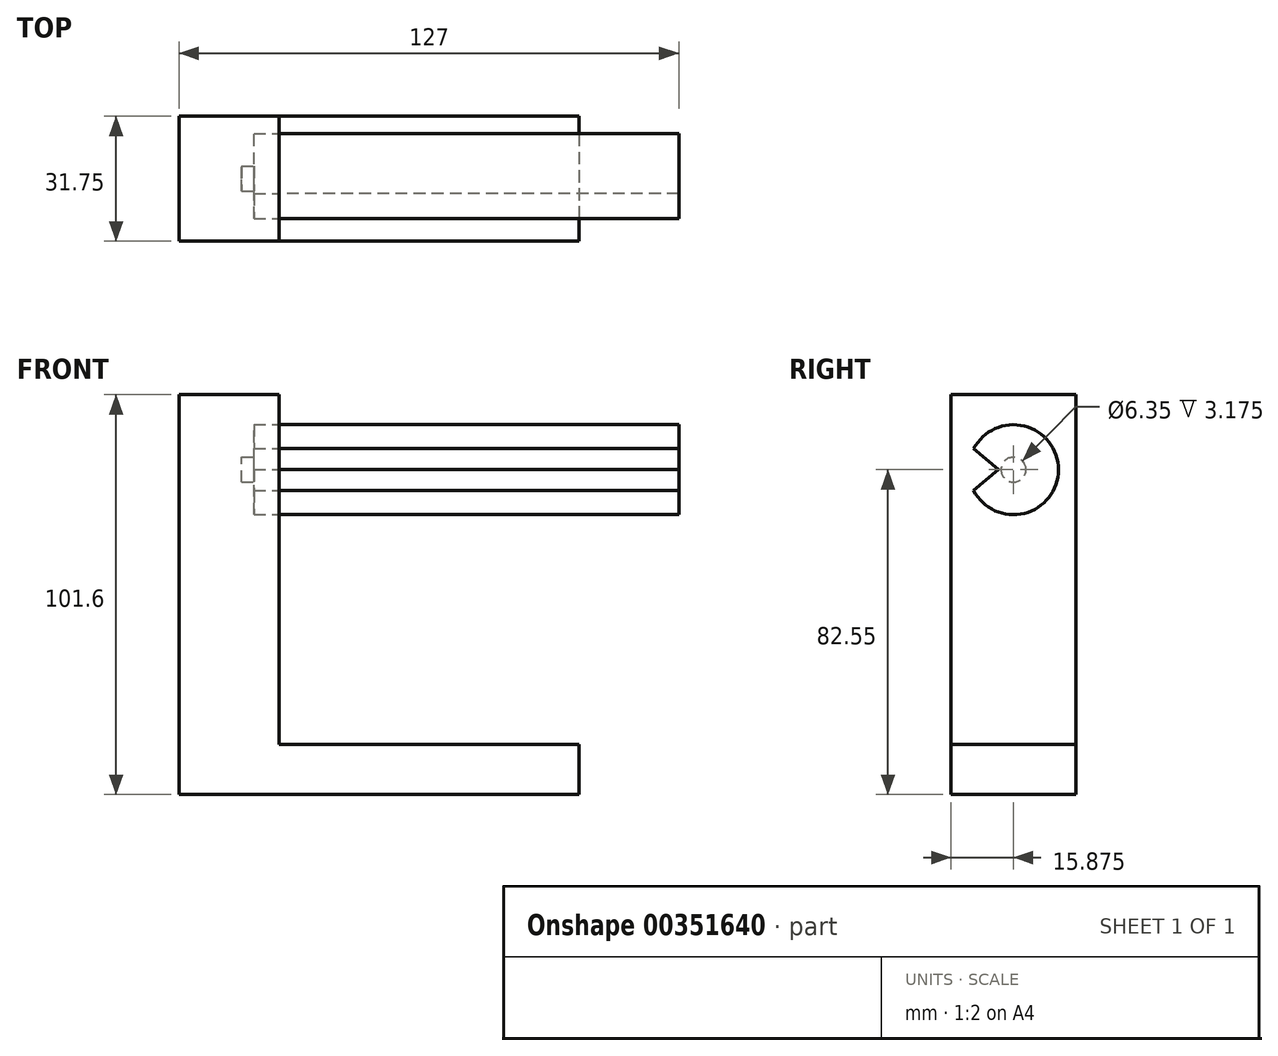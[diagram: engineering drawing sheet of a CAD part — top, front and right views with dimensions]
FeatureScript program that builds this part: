
annotation { "Feature Type Name" : "Feature", "Feature Type Description" : "" }
export const myFeature = defineFeature(function(context is Context, id is Id, definition is map)
    precondition{}
    {
        {
            var Q0;
            Q0=qCreatedBy(makeId("Right.planeOp"),FACE);
            var sketch = newSketch(context, id + "F0", { "sketchPlane" : qUnion([Q0])});
            skLineSegment(sketch, "E0.bottom", {"start": v(0, 0) * mm, "end": v(31.75, 0) * mm});
            skLineSegment(sketch, "E0.top", {"start": v(0, 101.6) * mm, "end": v(31.75, 101.6) * mm});
            skLineSegment(sketch, "E0.left", {"start": v(0, 0) * mm, "end": v(0, 101.6) * mm});
            skLineSegment(sketch, "E0.right", {"start": v(31.75, 0) * mm, "end": v(31.75, 101.6) * mm});
            skSolve(sketch);
        }
        {
            var Q0;
            Q0=qSketchRegion(id+"F0",true);
            extrude(context, id + "F1", {"entities" : qUnion([Q0]), "oppositeDirection" : true, "depth" : 25.4 * mm});
        }
        {
            var Q0;
            Q0=makeQuery(id+"F1.opExtrude","CAP_FACE",FACE,{"disambiguationData":[OSD([sQuery(id+"F0.wireOp",EDGE,"E0.bottom"),sQuery(id+"F0.wireOp",EDGE,"E0.top"),sQuery(id+"F0.wireOp",EDGE,"E0.left"),sQuery(id+"F0.wireOp",EDGE,"E0.right")])],"isStart":true});
            var sketch = newSketch(context, id + "F2", { "sketchPlane" : qUnion([Q0])});
            skArc(sketch, "E1", {"start": v(5.77, 77.21) * mm, "mid": v(27.3, 82.55) * mm, "end": v(5.77, 87.89) * mm});
            skPoint(sketch, "E2", {"position": v(12.06, 82.55) * mm});
            skLineSegment(sketch, "E3", {"start": v(12.06, 82.55) * mm, "end": v(5.77, 87.89) * mm});
            skLineSegment(sketch, "E4", {"start": v(12.06, 82.55) * mm, "end": v(5.77, 77.21) * mm});
            skSolve(sketch);
        }
        {
            var Q0;
            Q0=qSketchRegion(id+"F2",true);
            extrude(context, id + "F3", {"entities" : qUnion([Q0]), "operationType" : NewBodyOperationType.REMOVE, "oppositeDirection" : true, "depth" : 6.35 * mm});
        }
        {
            var Q0;
            Q0=makeQuery(id+"F3.boolean.opBoolean","COPY",FACE,{"derivedFrom":makeQuery(id+"F3.opExtrude","CAP_FACE",FACE,{"disambiguationData":[OSD([sQuery(id+"F2.wireOp",EDGE,"E1")])],"isStart":false})});
            var sketch = newSketch(context, id + "F4", { "sketchPlane" : qUnion([Q0])});
            skCircle(sketch, "E5", {"center": v(15.88, 82.55) * mm, "radius": 3.18 * mm});
            skSolve(sketch);
        }
        {
            var Q0;
            Q0=qSketchRegion(id+"F4",true);
            extrude(context, id + "F5", {"entities" : qUnion([Q0]), "operationType" : NewBodyOperationType.REMOVE, "oppositeDirection" : true, "depth" : 3.17 * mm});
        }
        {
            var Q0;
            Q0=makeQuery(id+"F1.opExtrude","SWEPT_FACE",FACE,{"disambiguationData":[OSD([sQuery(id+"F0.wireOp",EDGE,"E0.left")])]});
            var sketch = newSketch(context, id + "F6", { "sketchPlane" : qUnion([Q0])});
            skLineSegment(sketch, "E6.bottom", {"start": v(0, 0) * mm, "end": v(76.2, 0) * mm});
            skLineSegment(sketch, "E6.top", {"start": v(0, 12.7) * mm, "end": v(76.2, 12.7) * mm});
            skLineSegment(sketch, "E6.left", {"start": v(0, 0) * mm, "end": v(0, 12.7) * mm});
            skLineSegment(sketch, "E6.right", {"start": v(76.2, 0) * mm, "end": v(76.2, 12.7) * mm});
            skSolve(sketch);
        }
        {
            var Q0;
            Q0=qSketchRegion(id+"F6",true);
            extrude(context, id + "F7", {"entities" : qUnion([Q0]), "operationType" : NewBodyOperationType.ADD, "oppositeDirection" : true, "depth" : 31.75 * mm});
        }
        {
            var Q0;
            Q0=makeQuery(id+"F2.imprint","IMPRINT",FACE,{"disambiguationData":[TD([[makeQuery(id+"F2.imprint","IMPRINT",EDGE,{"derivedFrom":sQuery(id+"F2.wireOp",EDGE,"E1")}),1.0]])]});
            extrude(context, id + "F8", {"entities" : qUnion([Q0]), "operationType" : NewBodyOperationType.ADD, "depth" : 101.6 * mm});
        }
    });
